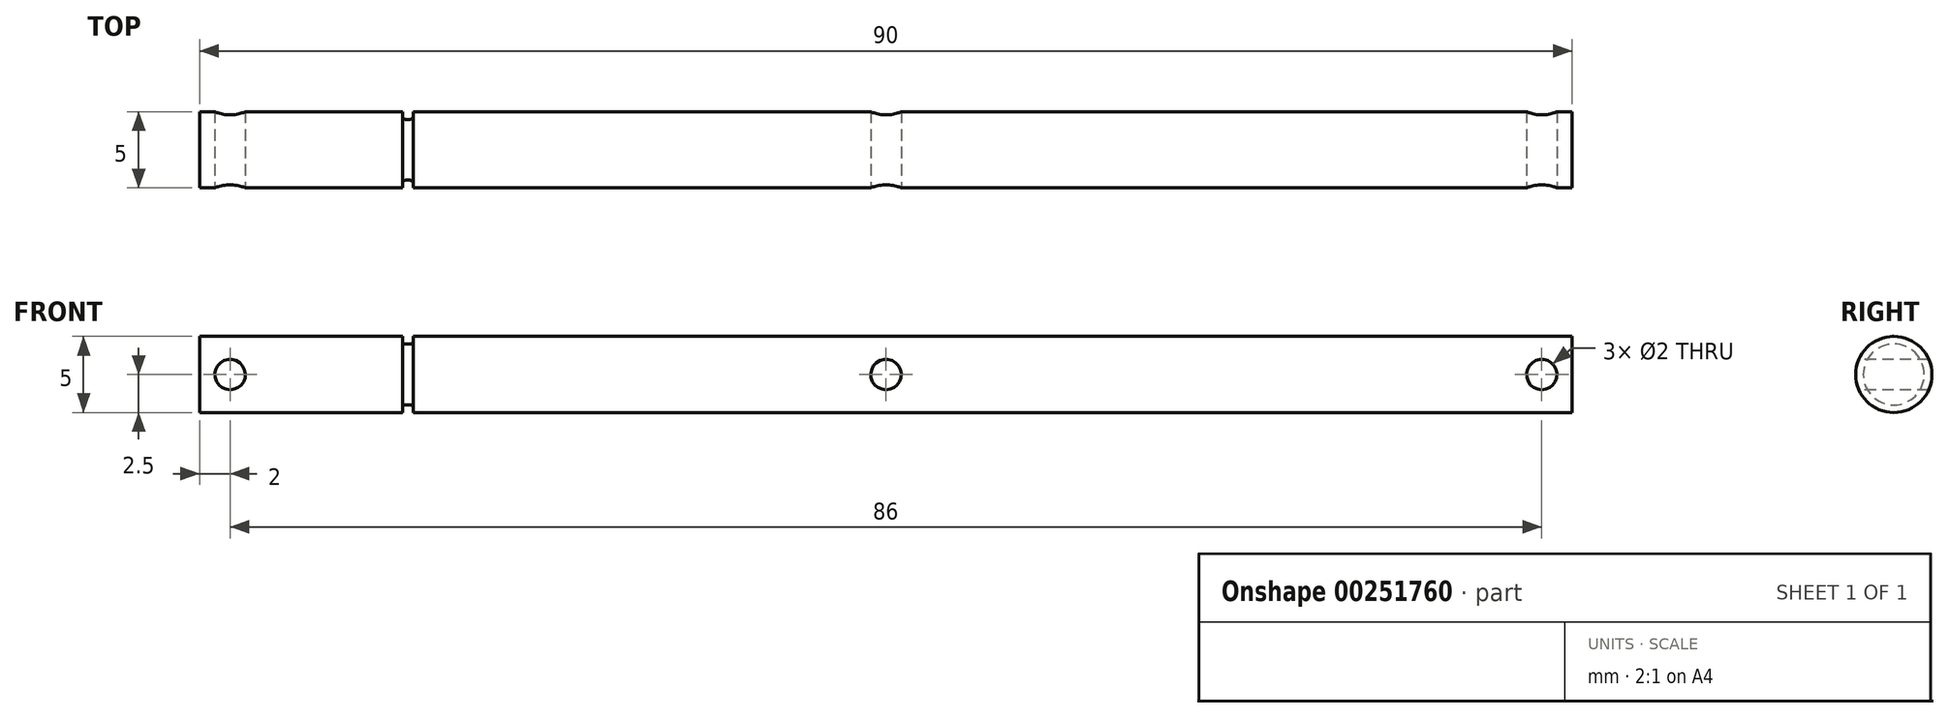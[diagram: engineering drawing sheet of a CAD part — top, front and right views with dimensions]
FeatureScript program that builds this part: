
annotation { "Feature Type Name" : "Feature", "Feature Type Description" : "" }
export const myFeature = defineFeature(function(context is Context, id is Id, definition is map)
    precondition{}
    {
        {
            var Q0;
            Q0=qCreatedBy(makeId("Front.planeOp"),FACE);
            var sketch = newSketch(context, id + "F0", { "sketchPlane" : qUnion([Q0])});
            skLineSegment(sketch, "E0.bottom", {"start": v(-45, 0) * mm, "end": v(45, 0) * mm});
            skLineSegment(sketch, "E0.top", {"start": v(-45, 2.5) * mm, "end": v(45, 2.5) * mm});
            skLineSegment(sketch, "E0.left", {"start": v(-45, 0) * mm, "end": v(-45, 2.5) * mm});
            skLineSegment(sketch, "E0.right", {"start": v(45, 0) * mm, "end": v(45, 2.5) * mm});
            skSolve(sketch);
        }
        {
            var Q0;
            Q0 = qSketchRegion(id + "F0", true);
            var Q1;
            Q1=sQuery(id+"F0.wireOp",EDGE,"E0.bottom");
            revolve(context, id + "F1", {"entities" : qUnion([Q0]), "axis" : qUnion([Q1]), "revolveType" : RevolveType.FULL});
        }
        {
            var Q0;
            Q0=qCreatedBy(makeId("Front.planeOp"),FACE);
            var sketch = newSketch(context, id + "F2", { "sketchPlane" : qUnion([Q0])});
            skCircle(sketch, "E1", {"center": v(-43, 0) * mm, "radius": 1 * mm});
            skCircle(sketch, "E2", {"center": v(0, 0) * mm, "radius": 1 * mm});
            skCircle(sketch, "E3", {"center": v(43, 0) * mm, "radius": 1 * mm});
            skSolve(sketch);
        }
        {
            var Q0;
            Q0 = qSketchRegion(id + "F2", true);
            extrude(context, id + "F3", {"entities" : qUnion([Q0]), "operationType" : NewBodyOperationType.REMOVE, "endBound" : BoundingType.SYMMETRIC, "oppositeDirection" : true, "depth" : 50 * mm});
        }
        {
            var Q0;
            Q0=qCreatedBy(makeId("Front.planeOp"),FACE);
            var sketch = newSketch(context, id + "F4", { "sketchPlane" : qUnion([Q0])});
            skLineSegment(sketch, "E4", {"start": v(-45, 2.5) * mm, "end": v(45, 2.5) * mm});
            skLineSegment(sketch, "E5", {"start": v(45, -2.5) * mm, "end": v(-45, -2.5) * mm});
            skLineSegment(sketch, "E6", {"start": v(-31.7, 2.5) * mm, "end": v(-31.7, 2.2) * mm});
            skLineSegment(sketch, "E7", {"start": v(-31.5, 2) * mm, "end": v(-31.2, 2) * mm});
            skLineSegment(sketch, "E8", {"start": v(-31, 2.2) * mm, "end": v(-31, 2.5) * mm});
            skPoint(sketch, "E9.visualSharp", {"position": v(-31.7, 2) * mm});
            skArc(sketch, "E9.filletArc", {"start": v(-31.7, 2.2) * mm, "mid": v(-31.64, 2.06) * mm, "end": v(-31.5, 2) * mm});
            skPoint(sketch, "E10.visualSharp", {"position": v(-31, 2) * mm});
            skArc(sketch, "E10.filletArc", {"start": v(-31.2, 2) * mm, "mid": v(-31.06, 2.06) * mm, "end": v(-31, 2.2) * mm});
            skLineSegment(sketch, "E11", {"start": v(-62.3, 0) * mm, "end": v(58.35, 0) * mm});
            skSolve(sketch);
        }
        {
            var Q0;
            Q0 = qSketchRegion(id + "F4", true);
            var Q1;
            Q1=sQuery(id+"F4.wireOp",EDGE,"E11");
            revolve(context, id + "F5", {"operationType" : NewBodyOperationType.REMOVE, "entities" : qUnion([Q0]), "axis" : qUnion([Q1]), "revolveType" : RevolveType.FULL, "oppositeDirection" : true});
        }
    });
